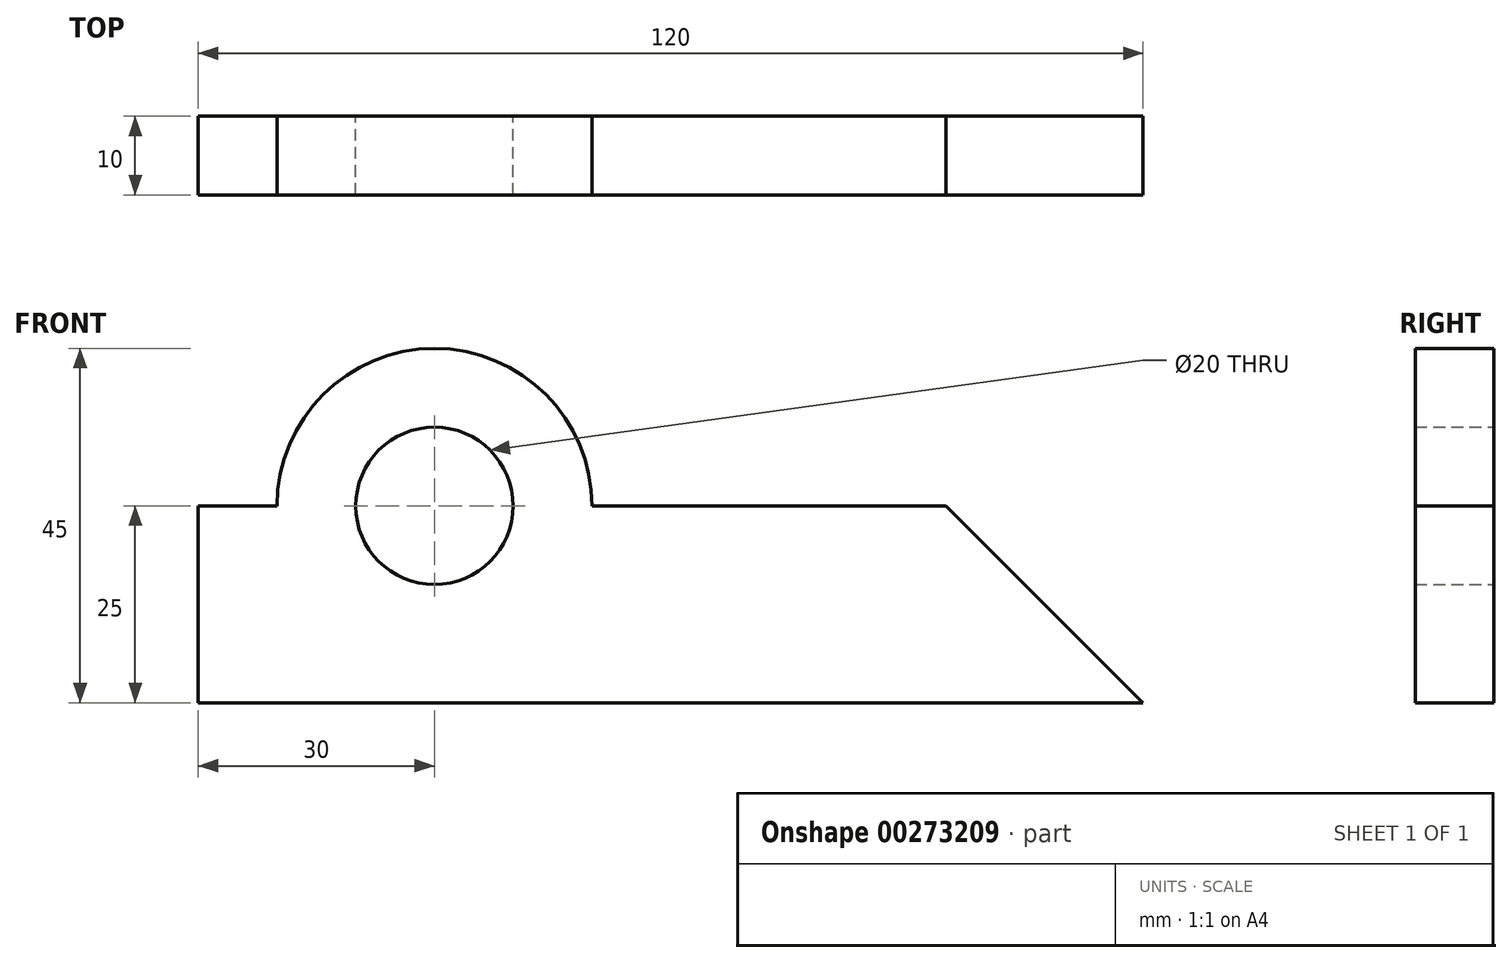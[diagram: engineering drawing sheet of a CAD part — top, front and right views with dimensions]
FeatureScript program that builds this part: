
annotation { "Feature Type Name" : "Feature", "Feature Type Description" : "" }
export const myFeature = defineFeature(function(context is Context, id is Id, definition is map)
    precondition{}
    {
        {
            var Q0;
            Q0=qCreatedBy(makeId("Front.planeOp"),FACE);
            var sketch = newSketch(context, id + "F0", { "sketchPlane" : qUnion([Q0])});
            skLineSegment(sketch, "E0", {"start": v(0, 0) * mm, "end": v(120, 0) * mm});
            skLineSegment(sketch, "E1", {"start": v(120, 0) * mm, "end": v(95, 25) * mm});
            skLineSegment(sketch, "E2", {"start": v(0, 0) * mm, "end": v(0, 25) * mm});
            skLineSegment(sketch, "E3", {"start": v(95, 25) * mm, "end": v(50, 25) * mm});
            skCircle(sketch, "E4", {"center": v(30, 25) * mm, "radius": 10 * mm});
            skLineSegment(sketch, "E5", {"start": v(0, 25) * mm, "end": v(10, 25) * mm});
            skArc(sketch, "E6", {"start": v(50, 25) * mm, "mid": v(30, 45) * mm, "end": v(10, 25) * mm});
            skSolve(sketch);
        }
        {
            var Q0;
            Q0 = qSketchRegion(id + "F0", true);
            extrude(context, id + "F1", {"entities" : qUnion([Q0]), "depth" : 10 * mm});
        }
    });
